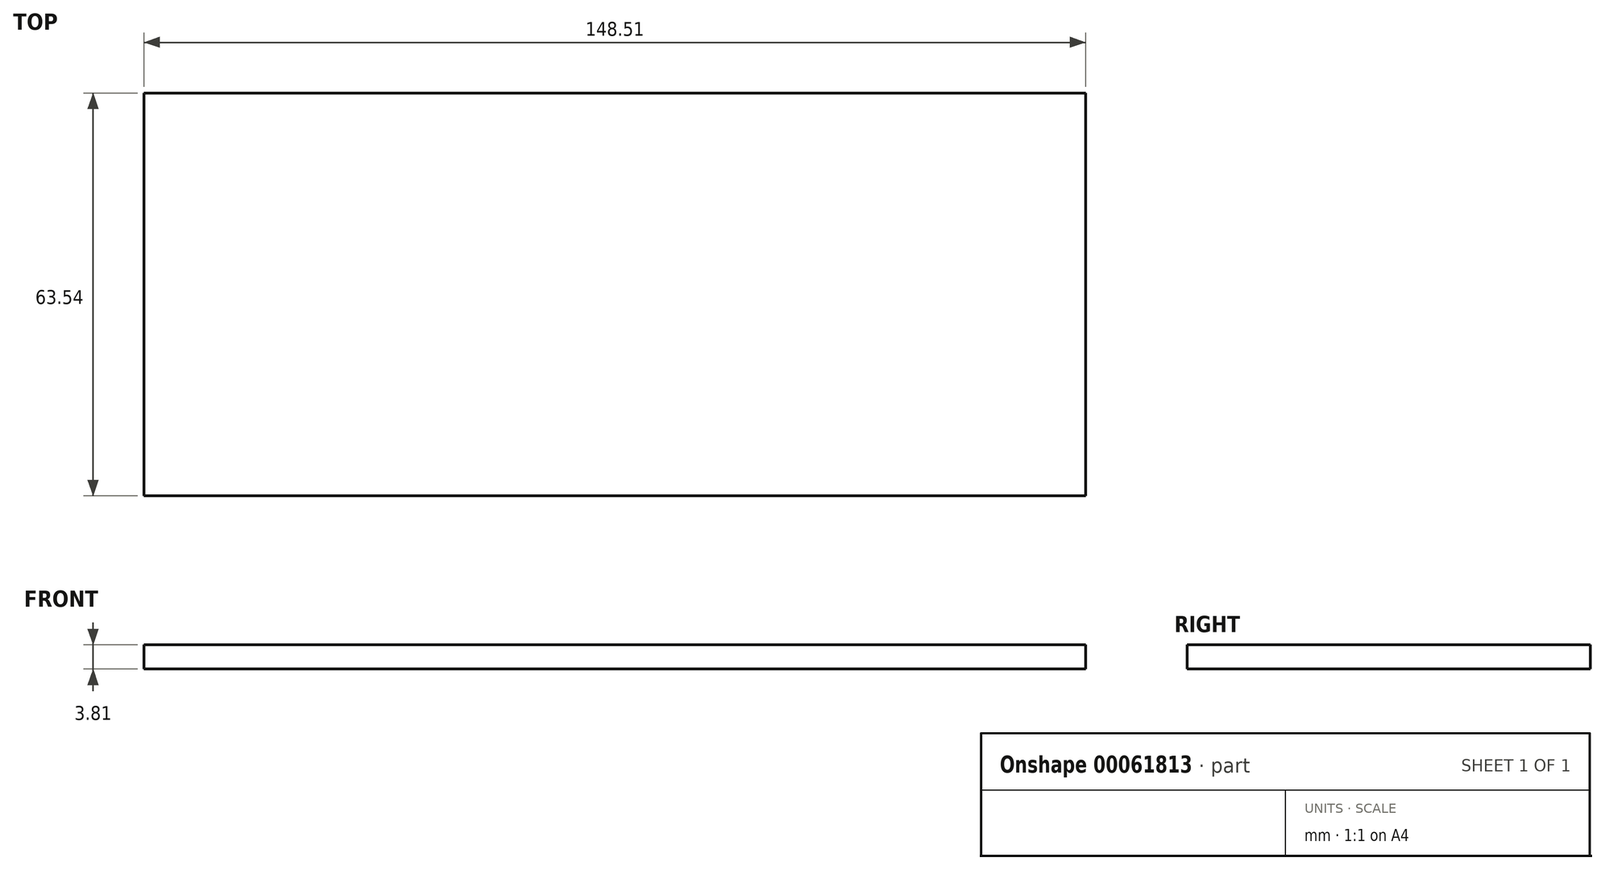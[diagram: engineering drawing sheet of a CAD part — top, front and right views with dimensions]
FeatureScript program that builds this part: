
annotation { "Feature Type Name" : "Feature", "Feature Type Description" : "" }
export const myFeature = defineFeature(function(context is Context, id is Id, definition is map)
    precondition{}
    {
        {
            var Q0;
            Q0=qCreatedBy(makeId("Top.planeOp"),FACE);
            var sketch = newSketch(context, id + "F0", { "sketchPlane" : qUnion([Q0])});
            skLineSegment(sketch, "E0.bottom", {"start": v(-73.9, 35.34) * mm, "end": v(74.6, 35.34) * mm});
            skLineSegment(sketch, "E0.top", {"start": v(-73.9, -28.2) * mm, "end": v(74.6, -28.2) * mm});
            skLineSegment(sketch, "E0.left", {"start": v(-73.9, 35.34) * mm, "end": v(-73.9, -28.2) * mm});
            skLineSegment(sketch, "E0.right", {"start": v(74.6, 35.34) * mm, "end": v(74.6, -28.2) * mm});
            skSolve(sketch);
        }
        {
            var Q0;
            Q0 = qSketchRegion(id + "F0", true);
            extrude(context, id + "F1", {"entities" : qUnion([Q0]), "depth" : 3.8 * mm});
        }
    });
